# Revit family: Door-Hydraulic-PowerLift-Standard_Frame-Small
name_source: partatom
category: Doors
units: mm (PartAtom-declared; Revit-internal decimal feet)

## family parameters
Always vertical = Yes
Classification Number = 23.30.10.00
Cut with Voids When Loaded = No
Host = Wall
Room Calculation Point = No
Shared = No

## types (58) — shared parameters
Analytic Construction = <None>
Description = Hydraulic Door - Standard Frame, Small Cylinder
Function = Exterior
Manufacturer = PowerLift Hydraulic Doors
Manufacturer Fax = 507-368-1358
Model = Standard Frame, Small Cylinder
URL = https://powerliftdoors.com
Wall Closure = By host

## per-type parameters (varying)
| type | Height | Rough Height | Rough Width | Width |
| 10'W x 16'H | 192 " | 192 " | 120 " | 120 " |
| 12'W x 16'H | 192 " | 192 " | 144 " | 144 " |
| 14'W x 16'H | 192 " | 192 " | 168 " | 168 " |
| 16'W x 16'H | 192 " | 192 " | 192 " | 192 " |
| 18'W x 16'H | 192 " | 192 " | 216 " | 216 " |
| 20'W x 16'H | 192 " | 192 " | 240 " | 240 " |
| 22'W x 16'H | 192 " | 192 " | 264 " | 264 " |
| 24'W x 16'H | 192 " | 192 " | 288 " | 288 " |
| 26'W x 16'H | 192 " | 192 " | 312 " | 312 " |
| 28'W x 16'H | 192 " | 192 " | 336 " | 336 " |
| 30'W x 14'H | 168 " | 168 " | 360 " | 360 " |
| 30'W x 16'H | 192 " | 192 " | 360 " | 360 " |
| 32'W x 8'H | 96 " | 96 " | 384 " | 384 " |
| 32'W x 10'H | 120 " | 120 " | 384 " | 384 " |
| 32'W x 12'H | 144 " | 144 " | 384 " | 384 " |
| 32'W x 14'H | 168 " | 168 " | 384 " | 384 " |
| 32'W x 16'H | 192 " | 192 " | 384 " | 384 " |
| 34'W x 8'H | 96 " | 96 " | 408 " | 408 " |
| 34'W x 10'H | 120 " | 120 " | 408 " | 408 " |
| 34'W x 12'H | 144 " | 144 " | 408 " | 408 " |
| 34'W x 14'H | 168 " | 168 " | 408 " | 408 " |
| 34'W x 16'H | 192 " | 192 " | 408 " | 408 " |
| 36'W x 8'H | 96 " | 96 " | 432 " | 432 " |
| 36'W x 10'H | 120 " | 120 " | 432 " | 432 " |
| 36'W x 12'H | 144 " | 144 " | 432 " | 432 " |
| 36'W x 14'H | 168 " | 168 " | 432 " | 432 " |
| 36'W x 16'H | 192 " | 192 " | 432 " | 432 " |
| 38'W x 8'H | 96 " | 96 " | 456 " | 456 " |
| 38'W x 10'H | 120 " | 120 " | 456 " | 456 " |
| 38'W x 12'H | 144 " | 144 " | 456 " | 456 " |
| 38'W x 14'H | 168 " | 168 " | 456 " | 456 " |
| 40'W x 8'H | 96 " | 96 " | 480 " | 480 " |
| 40'W x 10'H | 120 " | 120 " | 480 " | 480 " |
| 40'W x 12'H | 144 " | 144 " | 480 " | 480 " |
| 40'W x 14'H | 168 " | 168 " | 480 " | 480 " |
| 42'W x 8'H | 96 " | 96 " | 504 " | 504 " |
| 42'W x 10'H | 120 " | 120 " | 504 " | 504 " |
| 42'W x 12'H | 144 " | 144 " | 504 " | 504 " |
| 44'W x 8'H | 96 " | 96 " | 528 " | 528 " |
| 44'W x 10'H | 120 " | 120 " | 528 " | 528 " |
| 44'W x 12'H | 144 " | 144 " | 528 " | 528 " |
| 46'W x 8'H | 96 " | 96 " | 552 " | 552 " |
| 46'W x 10'H | 120 " | 120 " | 552 " | 552 " |
| 46'W x 12'H | 144 " | 144 " | 552 " | 552 " |
| 48'W x 8'H | 96 " | 96 " | 576 " | 576 " |
| 48'W x 10'H | 120 " | 120 " | 576 " | 576 " |
| 48'W x 12'H | 144 " | 144 " | 576 " | 576 " |
| 50'W x 8'H | 96 " | 96 " | 600 " | 600 " |
| 50'W x 10'H | 120 " | 120 " | 600 " | 600 " |
| 52'W x 8'H | 96 " | 96 " | 624 " | 624 " |
| 52'W x 10'H | 120 " | 120 " | 624 " | 624 " |
| 54'W x 8'H | 96 " | 96 " | 648 " | 648 " |
| 54'W x 10'H | 120 " | 120 " | 648 " | 648 " |
| 56'W x 8'H | 96 " | 96 " | 672 " | 672 " |
| 56'W x 10'H | 120 " | 120 " | 672 " | 672 " |
| 58'W x 8'H | 96 " | 96 " | 696 " | 696 " |
| 58'W x 10'H | 120 " | 120 " | 696 " | 696 " |
| 60'W x 8'H | 96 " | 96 " | 720 " | 720 " |

## geometry (parser evidence)
native form markers: Sweep x15
no freeform markers — native parametric forms only
